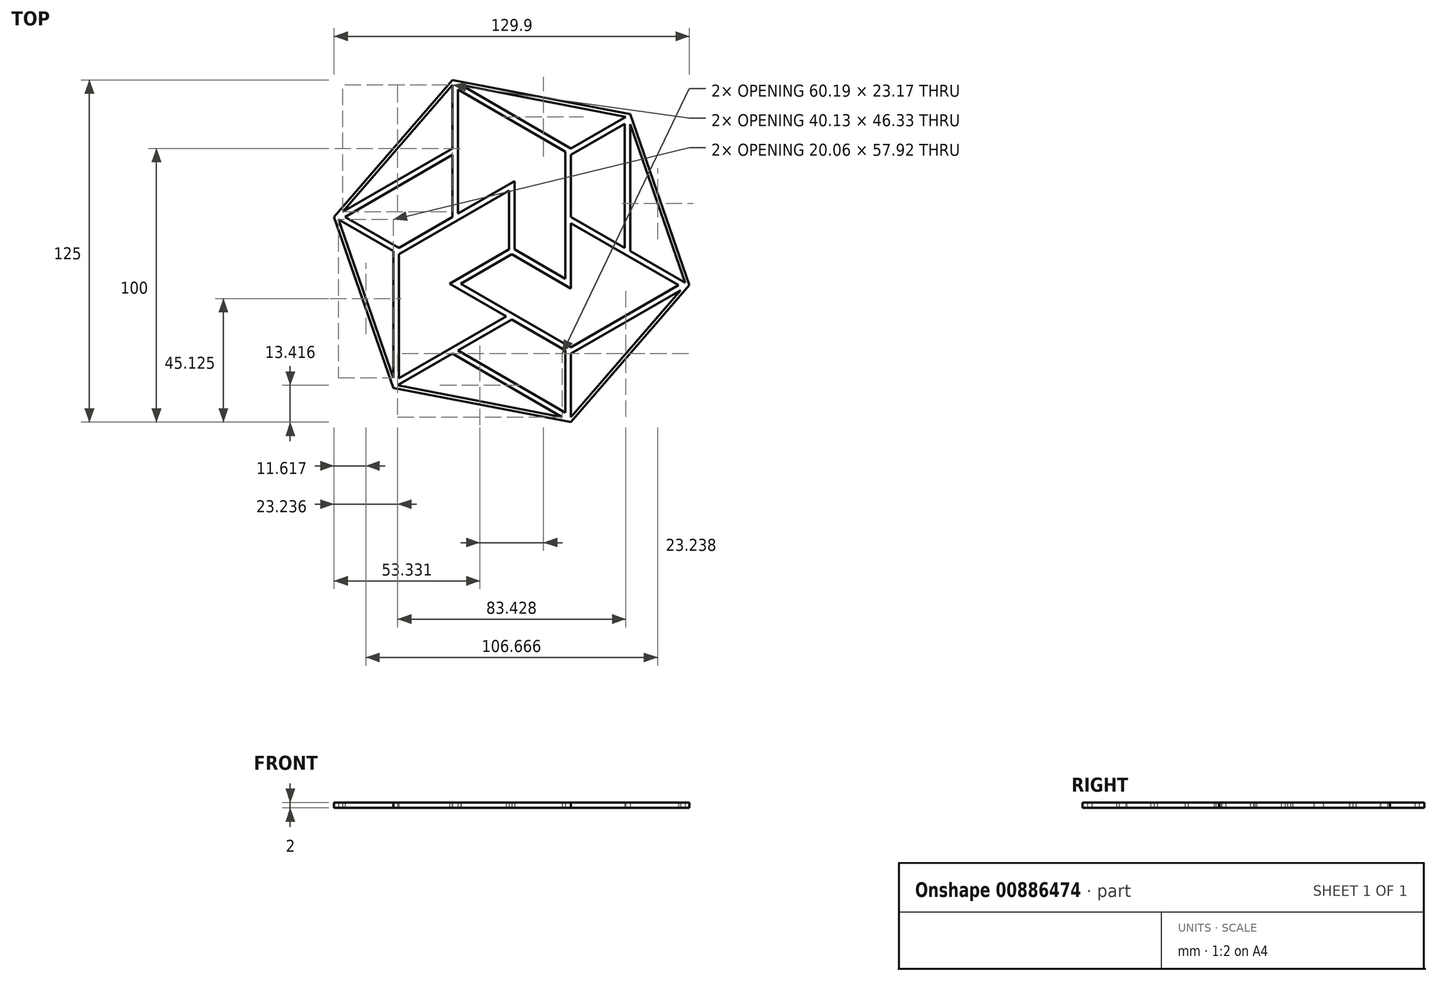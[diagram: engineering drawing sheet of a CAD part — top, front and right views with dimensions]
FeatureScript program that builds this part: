
annotation { "Feature Type Name" : "Feature", "Feature Type Description" : "" }
export const myFeature = defineFeature(function(context is Context, id is Id, definition is map)
    precondition{}
    {
        {
            var Q0;
            Q0=qCreatedBy(makeId("Top.planeOp"),FACE);
            var sketch = newSketch(context, id + "F0", { "sketchPlane" : qUnion([Q0])});
            skLineSegment(sketch, "E0", {"start": v(64.95, -12.5) * mm, "end": v(43.3, 0) * mm});
            skLineSegment(sketch, "E1", {"start": v(-21.65, 37.5) * mm, "end": v(-64.95, 12.5) * mm});
            skLineSegment(sketch, "E2", {"start": v(-64.95, 12.5) * mm, "end": v(-43.3, 0) * mm});
            skLineSegment(sketch, "E3", {"start": v(21.65, -37.5) * mm, "end": v(64.95, -12.5) * mm});
            skLineSegment(sketch, "E4.0", {"start": v(-21.65, 35.2) * mm, "end": v(-60.95, 12.5) * mm});
            skLineSegment(sketch, "E4.1", {"start": v(60.95, -12.5) * mm, "end": v(21.65, 10.2) * mm});
            skLineSegment(sketch, "E4.2", {"start": v(21.65, -35.2) * mm, "end": v(60.95, -12.5) * mm});
            skLineSegment(sketch, "E4.3", {"start": v(-60.95, 12.5) * mm, "end": v(-41.3, 1.15) * mm});
            skLineSegment(sketch, "E5.1", {"start": v(-2, 0) * mm, "end": v(-22.65, -11.92) * mm});
            skLineSegment(sketch, "E6.0", {"start": v(0, -1.15) * mm, "end": v(-18.65, -11.92) * mm});
            skLineSegment(sketch, "E6.1", {"start": v(0, -1.15) * mm, "end": v(21.65, -13.65) * mm});
            skLineSegment(sketch, "E7.0", {"start": v(2, 0) * mm, "end": v(19.65, -10.2) * mm});
            skLineSegment(sketch, "E8.1.0", {"start": v(1, 0.58) * mm, "end": v(1, 25.58) * mm});
            skLineSegment(sketch, "E8.1.1", {"start": v(21.65, -62.5) * mm, "end": v(21.65, -37.5) * mm});
            skLineSegment(sketch, "E8.1.3", {"start": v(-21.65, 62.5) * mm, "end": v(-21.65, 37.5) * mm});
            skLineSegment(sketch, "E8.1.5", {"start": v(-1, 1.73) * mm, "end": v(-1, 22.11) * mm});
            skLineSegment(sketch, "E8.1.6", {"start": v(19.65, 36.35) * mm, "end": v(-19.65, 59.04) * mm});
            skLineSegment(sketch, "E8.1.9", {"start": v(19.65, -59.04) * mm, "end": v(19.65, -36.35) * mm});
            skLineSegment(sketch, "E8.1.10", {"start": v(-21.65, -37.5) * mm, "end": v(21.65, -62.5) * mm});
            skLineSegment(sketch, "E8.1.12", {"start": v(1, 0.58) * mm, "end": v(19.65, -10.2) * mm});
            skLineSegment(sketch, "E8.1.13", {"start": v(21.65, 37.5) * mm, "end": v(-21.65, 62.5) * mm});
            skLineSegment(sketch, "E8.1.14", {"start": v(-19.65, -36.35) * mm, "end": v(19.65, -59.04) * mm});
            skLineSegment(sketch, "E8.1.15", {"start": v(-19.65, 59.04) * mm, "end": v(-19.65, 13.65) * mm});
            skLineSegment(sketch, "E8.2.0", {"start": v(-1, 0.58) * mm, "end": v(-22.65, -11.92) * mm});
            skLineSegment(sketch, "E8.2.1", {"start": v(43.3, 50) * mm, "end": v(21.65, 37.5) * mm});
            skLineSegment(sketch, "E8.2.3", {"start": v(-43.3, -50) * mm, "end": v(-21.65, -37.5) * mm});
            skLineSegment(sketch, "E8.2.5", {"start": v(-1, -1.73) * mm, "end": v(-18.65, -11.92) * mm});
            skLineSegment(sketch, "E8.2.6", {"start": v(-41.3, -1.15) * mm, "end": v(-41.3, -46.54) * mm});
            skLineSegment(sketch, "E8.2.7", {"start": v(1, 1.73) * mm, "end": v(1, 25.58) * mm});
            skLineSegment(sketch, "E8.2.9", {"start": v(41.3, 46.54) * mm, "end": v(21.65, 35.2) * mm});
            skLineSegment(sketch, "E8.2.10", {"start": v(43.3, 0) * mm, "end": v(43.3, 50) * mm});
            skLineSegment(sketch, "E8.2.12", {"start": v(-1, 0.58) * mm, "end": v(-1, 22.11) * mm});
            skLineSegment(sketch, "E8.2.13", {"start": v(-43.3, 0) * mm, "end": v(-43.3, -50) * mm});
            skLineSegment(sketch, "E8.2.14", {"start": v(41.3, 1.15) * mm, "end": v(41.3, 46.54) * mm});
            skLineSegment(sketch, "E8.2.15", {"start": v(-41.3, -46.54) * mm, "end": v(-2, -23.85) * mm});
            skPoint(sketch, "E8.center", {"position": v(0, 0) * mm});
            skLineSegment(sketch, "E9.trimOffspring", {"start": v(1, 25.58) * mm, "end": v(-19.65, 13.65) * mm});
            skLineSegment(sketch, "E10.trimOffspring", {"start": v(-1, 22.11) * mm, "end": v(-41.3, -1.15) * mm});
            skLineSegment(sketch, "E11.trimOffspring", {"start": v(21.65, -13.65) * mm, "end": v(21.65, 10.2) * mm});
            skLineSegment(sketch, "E12.trimOffspring", {"start": v(19.65, -10.2) * mm, "end": v(19.65, 36.35) * mm});
            skLineSegment(sketch, "E13.trimOffspring", {"start": v(-22.65, -11.92) * mm, "end": v(-2, -23.85) * mm});
            skLineSegment(sketch, "E14.trimOffspring", {"start": v(-21.65, 35.2) * mm, "end": v(-21.65, 12.5) * mm});
            skLineSegment(sketch, "E15.trimOffspring", {"start": v(-21.65, 12.5) * mm, "end": v(-41.3, 1.15) * mm});
            skLineSegment(sketch, "E16.trimOffspring", {"start": v(21.65, 12.5) * mm, "end": v(21.65, 35.2) * mm});
            skLineSegment(sketch, "E17.trimOffspring", {"start": v(0, -25) * mm, "end": v(19.65, -36.35) * mm});
            skLineSegment(sketch, "E18.trimOffspring", {"start": v(-18.65, -11.92) * mm, "end": v(21.65, -35.2) * mm});
            skLineSegment(sketch, "E19.trimOffspring", {"start": v(-19.65, -36.35) * mm, "end": v(0, -25) * mm});
            skLineSegment(sketch, "E20.trimOffspring", {"start": v(41.3, 1.15) * mm, "end": v(21.65, 12.5) * mm});
            skCircle(sketch, "E21.cCircle", {"center": v(0, 0) * mm, "radius": 66.14 * mm, "construction": true});
            skLineSegment(sketch, "E21.0", {"start": v(-64.95, 12.5) * mm, "end": v(-21.65, 62.5) * mm});
            skLineSegment(sketch, "E21.1", {"start": v(-21.65, 62.5) * mm, "end": v(43.3, 50) * mm});
            skLineSegment(sketch, "E21.2", {"start": v(43.3, 50) * mm, "end": v(64.95, -12.5) * mm});
            skLineSegment(sketch, "E21.3", {"start": v(64.95, -12.5) * mm, "end": v(21.65, -62.5) * mm});
            skLineSegment(sketch, "E21.4", {"start": v(21.65, -62.5) * mm, "end": v(-43.3, -50) * mm});
            skLineSegment(sketch, "E21.5", {"start": v(-43.3, -50) * mm, "end": v(-64.95, 12.5) * mm});
            skLineSegment(sketch, "E22.0", {"start": v(-42.4, -48.95) * mm, "end": v(-63.6, 12.24) * mm});
            skLineSegment(sketch, "E22.1", {"start": v(-21.2, 61.2) * mm, "end": v(42.4, 48.95) * mm});
            skLineSegment(sketch, "E22.2", {"start": v(42.4, 48.95) * mm, "end": v(63.6, -12.24) * mm});
            skLineSegment(sketch, "E22.3", {"start": v(-63.6, 12.24) * mm, "end": v(-21.2, 61.2) * mm});
            skLineSegment(sketch, "E22.4", {"start": v(63.6, -12.24) * mm, "end": v(21.2, -61.2) * mm});
            skLineSegment(sketch, "E22.5", {"start": v(21.2, -61.2) * mm, "end": v(-42.4, -48.95) * mm});
            skLineSegment(sketch, "E23.direction1", {"start": v(-60.95, 12.5) * mm, "end": v(-59.24, 13.49) * mm, "construction": true});
            skLineSegment(sketch, "E24", {"start": v(-21.65, 35.2) * mm, "end": v(-21.65, 35.2) * mm});
            skPoint(sketch, "E25.orphan", {"position": v(1.85, -0.08) * mm});
            skSolve(sketch);
        }
        {
            var Q0;
            Q0=makeQuery(id+"F0.imprint","IMPRINT",FACE,{"disambiguationData":[TD([[makeQuery(id+"F0.imprint","IMPRINT",EDGE,{"derivedFrom":sQuery(id+"F0.wireOp",EDGE,"E4.0")}),-1.0]])]});
            var Q1;
            {var subQ0=sQuery(id+"F0.wireOp",EDGE,"E21.0");Q1=makeQuery(id+"F0.imprint","IMPRINT",FACE,{"disambiguationData":[TD([[makeQuery(id+"F0.imprint","IMPRINT",EDGE,{"derivedFrom":subQ0}),-1.0]])]});}
            var Q2;
            {var subQ0=sQuery(id+"F0.wireOp",EDGE,"E21.1");Q2=makeQuery(id+"F0.imprint","IMPRINT",FACE,{"disambiguationData":[TD([[makeQuery(id+"F0.imprint","IMPRINT",EDGE,{"derivedFrom":subQ0}),-1.0]])]});}
            var Q3;
            {var subQ0=sQuery(id+"F0.wireOp",EDGE,"E21.5");Q3=makeQuery(id+"F0.imprint","IMPRINT",FACE,{"disambiguationData":[TD([[makeQuery(id+"F0.imprint","IMPRINT",EDGE,{"derivedFrom":subQ0}),-1.0]])]});}
            var Q4;
            {var subQ3=sQuery(id+"F0.wireOp",EDGE,"E22.3");var subQ5=sQuery(id+"F0.wireOp",EDGE,"E22.0");var subQ7=makeQuery(id+"F0.imprint","INTERSECT",VERTEX,{"derivedFrom":[subQ5,subQ3]});Q4=makeQuery(id+"F0.imprint","IMPRINT",FACE,{"disambiguationData":[TD([[makeQuery(id+"F0.imprint","IMPRINT",EDGE,{"disambiguationData":[TD([[subQ7,1.0]])],"derivedFrom":subQ5}),1.0]])]});}
            var Q5;
            {var subQ3=sQuery(id+"F0.wireOp",EDGE,"E22.5");var subQ5=sQuery(id+"F0.wireOp",EDGE,"E22.0");var subQ7=makeQuery(id+"F0.imprint","INTERSECT",VERTEX,{"derivedFrom":[subQ5,subQ3]});Q5=makeQuery(id+"F0.imprint","IMPRINT",FACE,{"disambiguationData":[TD([[makeQuery(id+"F0.imprint","IMPRINT",EDGE,{"disambiguationData":[TD([[subQ7,-1.0]])],"derivedFrom":subQ5}),1.0]])]});}
            var Q6;
            {var subQ0=sQuery(id+"F0.wireOp",EDGE,"E21.4");Q6=makeQuery(id+"F0.imprint","IMPRINT",FACE,{"disambiguationData":[TD([[makeQuery(id+"F0.imprint","IMPRINT",EDGE,{"derivedFrom":subQ0}),-1.0]])]});}
            var Q7;
            {var subQ3=sQuery(id+"F0.wireOp",EDGE,"E22.4");var subQ5=sQuery(id+"F0.wireOp",EDGE,"E22.5");var subQ6=makeQuery(id+"F0.imprint","INTERSECT",VERTEX,{"derivedFrom":[subQ3,subQ5]});Q7=makeQuery(id+"F0.imprint","IMPRINT",FACE,{"disambiguationData":[TD([[makeQuery(id+"F0.imprint","IMPRINT",EDGE,{"disambiguationData":[TD([[subQ6,1.0]])],"derivedFrom":subQ3}),1.0]])]});}
            var Q8;
            {var subQ0=sQuery(id+"F0.wireOp",EDGE,"E21.3");Q8=makeQuery(id+"F0.imprint","IMPRINT",FACE,{"disambiguationData":[TD([[makeQuery(id+"F0.imprint","IMPRINT",EDGE,{"derivedFrom":subQ0}),-1.0]])]});}
            var Q9;
            {var subQ3=sQuery(id+"F0.wireOp",EDGE,"E22.2");var subQ5=sQuery(id+"F0.wireOp",EDGE,"E22.4");var subQ7=makeQuery(id+"F0.imprint","INTERSECT",VERTEX,{"derivedFrom":[subQ3,subQ5]});Q9=makeQuery(id+"F0.imprint","IMPRINT",FACE,{"disambiguationData":[TD([[makeQuery(id+"F0.imprint","IMPRINT",EDGE,{"disambiguationData":[TD([[subQ7,1.0]])],"derivedFrom":subQ3}),1.0]])]});}
            var Q10;
            {var subQ0=sQuery(id+"F0.wireOp",EDGE,"E21.2");Q10=makeQuery(id+"F0.imprint","IMPRINT",FACE,{"disambiguationData":[TD([[makeQuery(id+"F0.imprint","IMPRINT",EDGE,{"derivedFrom":subQ0}),-1.0]])]});}
            var Q11;
            {var subQ3=sQuery(id+"F0.wireOp",EDGE,"E22.1");var subQ5=sQuery(id+"F0.wireOp",EDGE,"E22.2");var subQ6=makeQuery(id+"F0.imprint","INTERSECT",VERTEX,{"derivedFrom":[subQ3,subQ5]});Q11=makeQuery(id+"F0.imprint","IMPRINT",FACE,{"disambiguationData":[TD([[makeQuery(id+"F0.imprint","IMPRINT",EDGE,{"disambiguationData":[TD([[subQ6,1.0]])],"derivedFrom":subQ3}),1.0]])]});}
            var Q12;
            {var subQ3=sQuery(id+"F0.wireOp",EDGE,"E22.3");var subQ5=sQuery(id+"F0.wireOp",EDGE,"E22.1");var subQ7=makeQuery(id+"F0.imprint","INTERSECT",VERTEX,{"derivedFrom":[subQ5,subQ3]});Q12=makeQuery(id+"F0.imprint","IMPRINT",FACE,{"disambiguationData":[TD([[makeQuery(id+"F0.imprint","IMPRINT",EDGE,{"disambiguationData":[TD([[subQ7,-1.0]])],"derivedFrom":subQ5}),1.0]])]});}
            var Q13;
            {var subQ0=sQuery(id+"F0.wireOp",EDGE,"E23.3.0.0");Q13=makeQuery(id+"F0.imprint","IMPRINT",FACE,{"disambiguationData":[TD([[makeQuery(id+"F0.imprint","IMPRINT",EDGE,{"derivedFrom":subQ0}),1.0]])]});}
            var Q14;
            {var subQ0=sQuery(id+"F0.wireOp",EDGE,"E23.7.0.0");Q14=makeQuery(id+"F0.imprint","IMPRINT",FACE,{"disambiguationData":[TD([[makeQuery(id+"F0.imprint","IMPRINT",EDGE,{"derivedFrom":subQ0}),1.0]])]});}
            var Q15;
            {var subQ0=sQuery(id+"F0.wireOp",EDGE,"E23.11.0.0");Q15=makeQuery(id+"F0.imprint","IMPRINT",FACE,{"disambiguationData":[TD([[makeQuery(id+"F0.imprint","IMPRINT",EDGE,{"derivedFrom":subQ0}),1.0]])]});}
            var Q16;
            {var subQ0=sQuery(id+"F0.wireOp",EDGE,"E23.15.0.0");Q16=makeQuery(id+"F0.imprint","IMPRINT",FACE,{"disambiguationData":[TD([[makeQuery(id+"F0.imprint","IMPRINT",EDGE,{"derivedFrom":subQ0}),1.0]])]});}
            var Q17;
            {var subQ0=sQuery(id+"F0.wireOp",EDGE,"E23.19.0.0");Q17=makeQuery(id+"F0.imprint","IMPRINT",FACE,{"disambiguationData":[TD([[makeQuery(id+"F0.imprint","IMPRINT",EDGE,{"derivedFrom":subQ0}),1.0]])]});}
            var Q18;
            {var subQ0=sQuery(id+"F0.wireOp",EDGE,"95564fad-a639-4184-878d-f1c2f7a62f20.3.0.0");Q18=makeQuery(id+"F0.imprint","IMPRINT",FACE,{"disambiguationData":[TD([[makeQuery(id+"F0.imprint","IMPRINT",EDGE,{"derivedFrom":subQ0}),1.0]])]});}
            var Q19;
            {var subQ0=sQuery(id+"F0.wireOp",EDGE,"95564fad-a639-4184-878d-f1c2f7a62f20.7.0.0");Q19=makeQuery(id+"F0.imprint","IMPRINT",FACE,{"disambiguationData":[TD([[makeQuery(id+"F0.imprint","IMPRINT",EDGE,{"derivedFrom":subQ0}),1.0]])]});}
            var Q20;
            {var subQ3=sQuery(id+"F0.wireOp",EDGE,"E24");Q20=makeQuery(id+"F0.imprint","IMPRINT",FACE,{"disambiguationData":[TD([[makeQuery(id+"F0.imprint","IMPRINT",EDGE,{"derivedFrom":subQ3}),-1.0]])]});}
            var Q21;
            {var subQ3=sQuery(id+"F0.wireOp",EDGE,"95564fad-a639-4184-878d-f1c2f7a62f20.12.0.0");Q21=makeQuery(id+"F0.imprint","IMPRINT",FACE,{"disambiguationData":[TD([[makeQuery(id+"F0.imprint","IMPRINT",EDGE,{"derivedFrom":subQ3}),-1.0]])]});}
            var Q22;
            {var subQ0=sQuery(id+"F0.wireOp",EDGE,"95564fad-a639-4184-878d-f1c2f7a62f20.15.0.0");Q22=makeQuery(id+"F0.imprint","IMPRINT",FACE,{"disambiguationData":[TD([[makeQuery(id+"F0.imprint","IMPRINT",EDGE,{"derivedFrom":subQ0}),1.0]])]});}
            var Q23;
            {var subQ0=sQuery(id+"F0.wireOp",EDGE,"95564fad-a639-4184-878d-f1c2f7a62f20.19.0.0");Q23=makeQuery(id+"F0.imprint","IMPRINT",FACE,{"disambiguationData":[TD([[makeQuery(id+"F0.imprint","IMPRINT",EDGE,{"derivedFrom":subQ0}),1.0]])]});}
            extrude(context, id + "F1", {"entities" : qUnion([Q0, Q1, Q2, Q3, Q4, Q5, Q6, Q7, Q8, Q9, Q10, Q11, Q12, Q13, Q14, Q15, Q16, Q17, Q18, Q19, Q20, Q21, Q22, Q23]), "depth" : 2 * mm, "offsetDistance" : 25 * mm});
        }
    });
